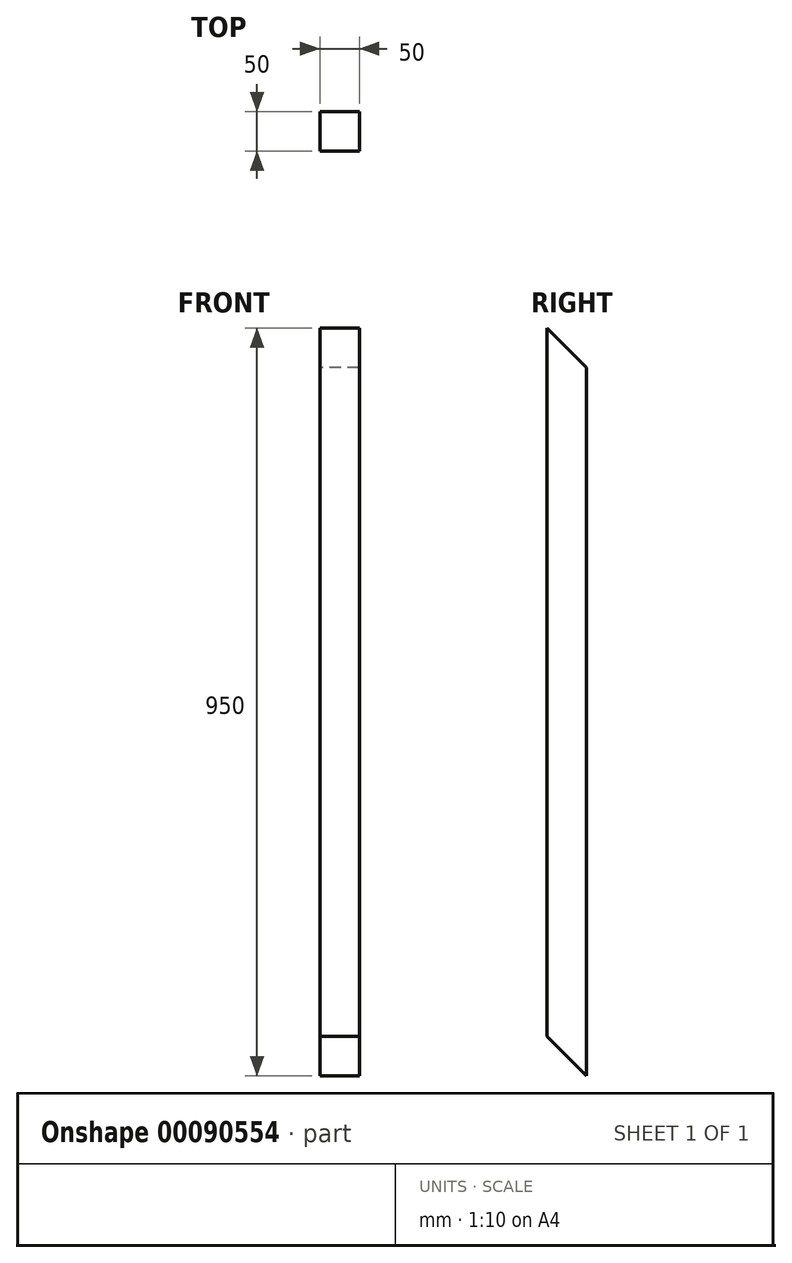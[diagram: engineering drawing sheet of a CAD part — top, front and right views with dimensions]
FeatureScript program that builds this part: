
annotation { "Feature Type Name" : "Feature", "Feature Type Description" : "" }
export const myFeature = defineFeature(function(context is Context, id is Id, definition is map)
    precondition{}
    {
        {
            var Q0;
            Q0=qCreatedBy(makeId("Top.planeOp"),FACE);
            var sketch = newSketch(context, id + "F0", { "sketchPlane" : qUnion([Q0])});
            skLineSegment(sketch, "E0.bottom", {"start": v(25, -25) * mm, "end": v(-25, -25) * mm});
            skLineSegment(sketch, "E0.top", {"start": v(25, 25) * mm, "end": v(-25, 25) * mm});
            skLineSegment(sketch, "E0.left", {"start": v(25, -25) * mm, "end": v(25, 25) * mm});
            skLineSegment(sketch, "E0.right", {"start": v(-25, -25) * mm, "end": v(-25, 25) * mm});
            skPoint(sketch, "E0.middle", {"position": v(0, 0) * mm});
            skSolve(sketch);
        }
        {
            var Q0;
            Q0=qSketchRegion(id+"F0",true);
            extrude(context, id + "F1", {"entities" : qUnion([Q0]), "depth" : 950 * mm});
        }
        {
            var Q0;
            Q0=qCreatedBy(makeId("Right.planeOp"),FACE);
            var sketch = newSketch(context, id + "F2", { "sketchPlane" : qUnion([Q0])});
            skLineSegment(sketch, "E1", {"start": v(-25, 950) * mm, "end": v(135.3, 950) * mm});
            skLineSegment(sketch, "E2", {"start": v(135.3, 950) * mm, "end": v(135.3, 789.7) * mm});
            skLineSegment(sketch, "E3", {"start": v(135.3, 789.7) * mm, "end": v(-25, 950) * mm});
            skSolve(sketch);
        }
        {
            var Q0;
            Q0=qSketchRegion(id+"F2",true);
            extrude(context, id + "F3", {"entities" : qUnion([Q0]), "operationType" : NewBodyOperationType.REMOVE, "endBound" : BoundingType.THROUGH_ALL, "oppositeDirection" : true, "depth" : 25 * mm, "hasSecondDirection" : true, "secondDirectionBound" : SecondDirectionBoundingType.THROUGH_ALL, "secondDirectionOppositeDirection" : false, "secondDirectionDepth" : 25 * mm});
        }
        {
            var Q0;
            Q0=qCreatedBy(makeId("Right.planeOp"),FACE);
            var sketch = newSketch(context, id + "F4", { "sketchPlane" : qUnion([Q0])});
            skLineSegment(sketch, "E4", {"start": v(25, 0) * mm, "end": v(-25, 50) * mm});
            skLineSegment(sketch, "E5", {"start": v(-25, 50) * mm, "end": v(-25, 0) * mm});
            skLineSegment(sketch, "E6", {"start": v(-25, 0) * mm, "end": v(25, 0) * mm});
            skSolve(sketch);
        }
        {
            var Q0;
            Q0=qSketchRegion(id+"F4",true);
            extrude(context, id + "F5", {"entities" : qUnion([Q0]), "operationType" : NewBodyOperationType.REMOVE, "endBound" : BoundingType.THROUGH_ALL, "oppositeDirection" : true, "depth" : 25 * mm, "hasSecondDirection" : true, "secondDirectionBound" : SecondDirectionBoundingType.THROUGH_ALL, "secondDirectionOppositeDirection" : false, "secondDirectionDepth" : 25 * mm});
        }
    });
